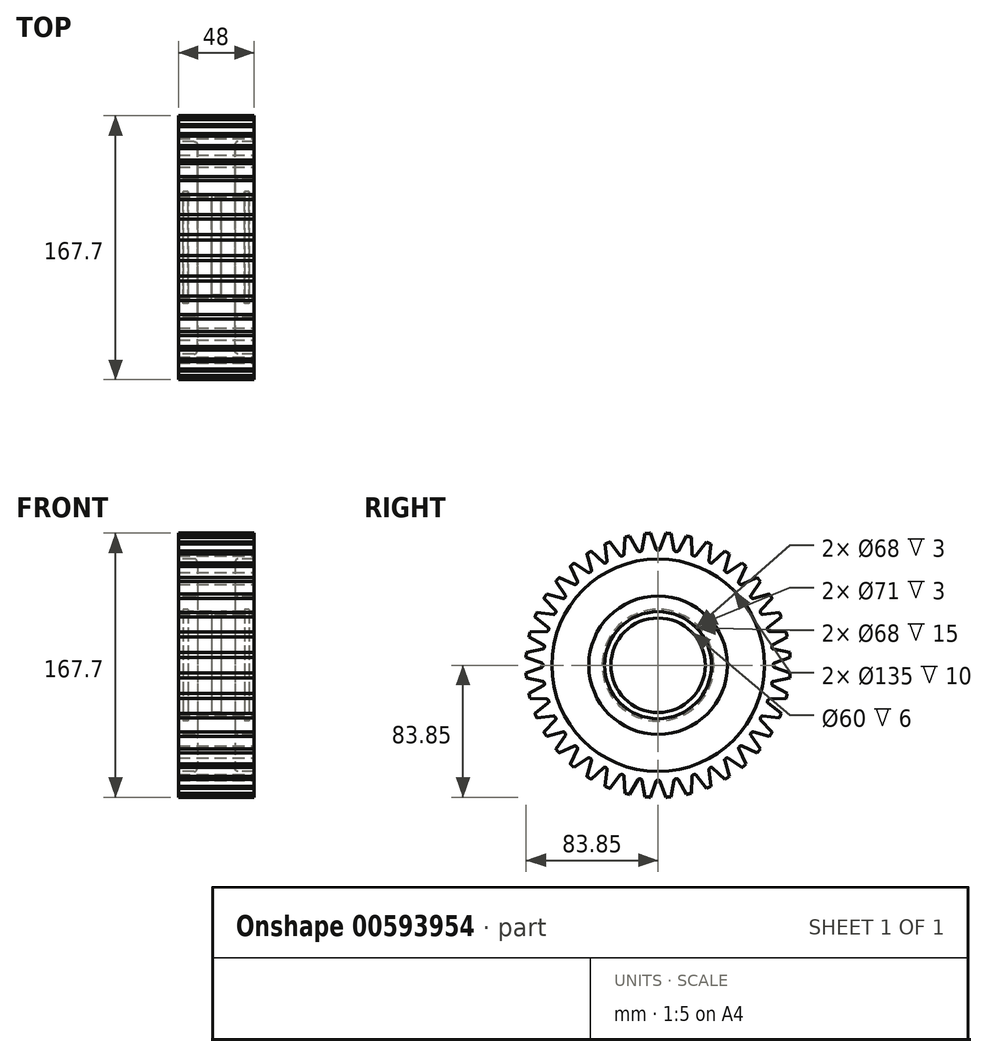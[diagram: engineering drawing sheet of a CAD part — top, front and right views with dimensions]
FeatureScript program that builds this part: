
annotation { "Feature Type Name" : "Feature", "Feature Type Description" : "" }
export const myFeature = defineFeature(function(context is Context, id is Id, definition is map)
    precondition{}
    {
        {
            var Q0;
            Q0=qCreatedBy(makeId("Front.planeOp"),FACE);
            var sketch = newSketch(context, id + "F0", { "sketchPlane" : qUnion([Q0])});
            skLineSegment(sketch, "E0.bottom", {"start": v(-24, 84) * mm, "end": v(0, 84) * mm});
            skLineSegment(sketch, "E0.top", {"start": v(-24, 0) * mm, "end": v(0, 0) * mm, "construction": true});
            skLineSegment(sketch, "E0.left", {"start": v(-24, 84) * mm, "end": v(-24, 67.5) * mm});
            skLineSegment(sketch, "E0.right", {"start": v(0, 84) * mm, "end": v(0, 0) * mm, "construction": true});
            skLineSegment(sketch, "E1", {"start": v(-24, 34) * mm, "end": v(-21, 34) * mm});
            skLineSegment(sketch, "E2", {"start": v(-21, 34) * mm, "end": v(-21, 35.5) * mm});
            skLineSegment(sketch, "E3", {"start": v(-21, 35.5) * mm, "end": v(-18, 35.5) * mm});
            skLineSegment(sketch, "E4", {"start": v(-18, 35.5) * mm, "end": v(-18, 34) * mm});
            skLineSegment(sketch, "E5", {"start": v(-18, 34) * mm, "end": v(-3, 34) * mm});
            skLineSegment(sketch, "E6", {"start": v(-3, 34) * mm, "end": v(-3, 30) * mm});
            skLineSegment(sketch, "E7", {"start": v(-3, 30) * mm, "end": v(0, 30) * mm});
            skLineSegment(sketch, "E8", {"start": v(-24, 67.5) * mm, "end": v(-14, 67.5) * mm});
            skLineSegment(sketch, "E9", {"start": v(-12, 65.5) * mm, "end": v(-12, 46) * mm});
            skLineSegment(sketch, "E10", {"start": v(-14, 44) * mm, "end": v(-24, 44) * mm});
            skLineSegment(sketch, "E11.trimOffspring", {"start": v(-24, 44) * mm, "end": v(-24, 34) * mm});
            skPoint(sketch, "E12.visualSharp", {"position": v(-12, 67.5) * mm});
            skArc(sketch, "E12.filletArc", {"start": v(-12, 65.5) * mm, "mid": v(-12.59, 66.91) * mm, "end": v(-14, 67.5) * mm});
            skPoint(sketch, "E13.visualSharp", {"position": v(-12, 44) * mm});
            skArc(sketch, "E13.filletArc", {"start": v(-14, 44) * mm, "mid": v(-12.59, 44.59) * mm, "end": v(-12, 46) * mm});
            skLineSegment(sketch, "E14.MirrorCS", {"start": v(24, 84) * mm, "end": v(0, 84) * mm});
            skLineSegment(sketch, "E15.MirrorCS", {"start": v(24, 84) * mm, "end": v(24, 67.5) * mm});
            skLineSegment(sketch, "E16.MirrorCS", {"start": v(24, 67.5) * mm, "end": v(14, 67.5) * mm});
            skArc(sketch, "E17.MirrorCS", {"start": v(12, 65.5) * mm, "mid": v(12.59, 66.91) * mm, "end": v(14, 67.5) * mm});
            skLineSegment(sketch, "E18.MirrorCS", {"start": v(12, 65.5) * mm, "end": v(12, 46) * mm});
            skArc(sketch, "E19.MirrorCS", {"start": v(14, 44) * mm, "mid": v(12.59, 44.59) * mm, "end": v(12, 46) * mm});
            skLineSegment(sketch, "E20.MirrorCS", {"start": v(14, 44) * mm, "end": v(24, 44) * mm});
            skLineSegment(sketch, "E21.MirrorCS", {"start": v(24, 44) * mm, "end": v(24, 34) * mm});
            skLineSegment(sketch, "E22.MirrorCS", {"start": v(24, 34) * mm, "end": v(21, 34) * mm});
            skLineSegment(sketch, "E23.MirrorCS", {"start": v(21, 34) * mm, "end": v(21, 35.5) * mm});
            skLineSegment(sketch, "E24.MirrorCS", {"start": v(21, 35.5) * mm, "end": v(18, 35.5) * mm});
            skLineSegment(sketch, "E25.MirrorCS", {"start": v(18, 35.5) * mm, "end": v(18, 34) * mm});
            skLineSegment(sketch, "E26.MirrorCS", {"start": v(18, 34) * mm, "end": v(3, 34) * mm});
            skLineSegment(sketch, "E27.MirrorCS", {"start": v(3, 34) * mm, "end": v(3, 30) * mm});
            skLineSegment(sketch, "E28.MirrorCS", {"start": v(3, 30) * mm, "end": v(0, 30) * mm});
            skSolve(sketch);
        }
        {
            var Q0;
            Q0=makeQuery(id+"F0.imprint","IMPRINT",FACE,{"disambiguationData":[TD([[makeQuery(id+"F0.imprint","IMPRINT",EDGE,{"derivedFrom":sQuery(id+"F0.wireOp",EDGE,"E0.bottom")}),-1.0]])]});
            var Q1;
            Q1=sQuery(id+"F0.wireOp",EDGE,"E0.top");
            revolve(context, id + "F1", {"entities" : qUnion([Q0]), "axis" : qUnion([Q1]), "revolveType" : RevolveType.FULL});
        }
        {
            var Q0;
            Q0=makeQuery(id+"F1.opRevolve","SWEPT_FACE",FACE,{"disambiguationData":[OSD([sQuery(id+"F0.wireOp",EDGE,"E15.MirrorCS")])]});
            var sketch = newSketch(context, id + "F2", { "sketchPlane" : qUnion([Q0])});
            skLineSegment(sketch, "E29", {"start": v(0, 0) * mm, "end": v(0, 91.72) * mm, "construction": true});
            skLineSegment(sketch, "E30", {"start": v(1.33, 73.81) * mm, "end": v(4.98, 83.85) * mm});
            skLineSegment(sketch, "E31.MirrorCS", {"start": v(-1.33, 73.81) * mm, "end": v(-4.98, 83.85) * mm});
            skLineSegment(sketch, "E32", {"start": v(-0.39, 73.15) * mm, "end": v(0.39, 73.15) * mm});
            skPoint(sketch, "E33.visualSharp", {"position": v(-1.09, 73.15) * mm});
            skArc(sketch, "E33.filletArc", {"start": v(-1.33, 73.81) * mm, "mid": v(-0.96, 73.33) * mm, "end": v(-0.39, 73.15) * mm});
            skPoint(sketch, "E34.visualSharp", {"position": v(1.09, 73.15) * mm});
            skArc(sketch, "E34.filletArc", {"start": v(0.39, 73.15) * mm, "mid": v(0.96, 73.33) * mm, "end": v(1.33, 73.81) * mm});
            skSolve(sketch);
        }
        {
            var Q0;
            Q0 = qSketchRegion(id + "F2", true);
            var Q1;
            {var subQ1=sQuery(id+"F2.wireOp",EDGE,"E30");Q1=makeQuery(id+"F2.imprint","IMPRINT",FACE,{"disambiguationData":[TD([[makeQuery(id+"F2.imprint","IMPRINT",EDGE,{"derivedFrom":subQ1}),1.0]])]});}
            extrude(context, id + "F3", {"entities" : qUnion([Q0, Q1]), "operationType" : NewBodyOperationType.REMOVE, "oppositeDirection" : true, "depth" : 50 * mm, "offsetDistance" : 25 * mm});
        }
        {
            var Q0;
            Q0=makeQuery(id+"F3.boolean.opBoolean","COPY",FACE,{"derivedFrom":makeQuery(id+"F3.opExtrude","SWEPT_FACE",FACE,{"disambiguationData":[OSD([sQuery(id+"F2.wireOp",EDGE,"E31.MirrorCS")])]})});
            var Q1;
            Q1=makeQuery(id+"F3.boolean.opBoolean","COPY",FACE,{"derivedFrom":makeQuery(id+"F3.opExtrude","SWEPT_FACE",FACE,{"disambiguationData":[OSD([sQuery(id+"F2.wireOp",EDGE,"E30")])]})});
            var Q2;
            Q2=makeQuery(id+"F3.boolean.opBoolean","COPY",FACE,{"derivedFrom":makeQuery(id+"F3.opExtrude","SWEPT_FACE",FACE,{"disambiguationData":[OSD([sQuery(id+"F2.wireOp",EDGE,"E34.filletArc")])]})});
            var Q3;
            Q3=makeQuery(id+"F3.boolean.opBoolean","COPY",FACE,{"derivedFrom":makeQuery(id+"F3.opExtrude","SWEPT_FACE",FACE,{"disambiguationData":[OSD([sQuery(id+"F2.wireOp",EDGE,"E32")])]})});
            var Q4;
            Q4=makeQuery(id+"F3.boolean.opBoolean","COPY",FACE,{"derivedFrom":makeQuery(id+"F3.opExtrude","SWEPT_FACE",FACE,{"disambiguationData":[OSD([sQuery(id+"F2.wireOp",EDGE,"E33.filletArc")])]})});
            var Q5;
            Q5=sQuery(id+"F0.wireOp",EDGE,"E0.top");
            circularPattern(context, id + "F4", {"patternType" : PatternType.FACE, "faces" : qUnion([Q0, Q1, Q2, Q3, Q4]), "axis" : qUnion([Q5]), "angle" : 9 * degree, "instanceCount" : 21, "oppositeDirection" : true, "isCentered" : true});
        }
    });
